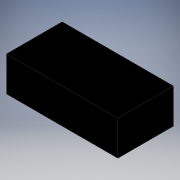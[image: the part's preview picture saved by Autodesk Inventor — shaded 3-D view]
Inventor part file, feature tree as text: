
AUTODESK INVENTOR PART (.ipt)
format: ipt  version: 2016 (Build 200138000, 138)  size: 91,648 bytes
history: native  units: in
note: dims shown in document units (in); Inventor stores cm internally (conversion verified against a paired STEP export)
features: extrude x1, sketch x1
ambient origin geometry x8: Origin, YZ Plane, XZ Plane, XY Plane, X Axis, Y Axis, Z Axis, Center Point
bodies: Solid1 (feature_tree)
feature tree (2):
  extrude  "Extrusion1"  Depth=1.25in
  sketch  "Sketch1"  dims[d0=4.0in d1=1.25in d2=2.0in d3=0.0in]
